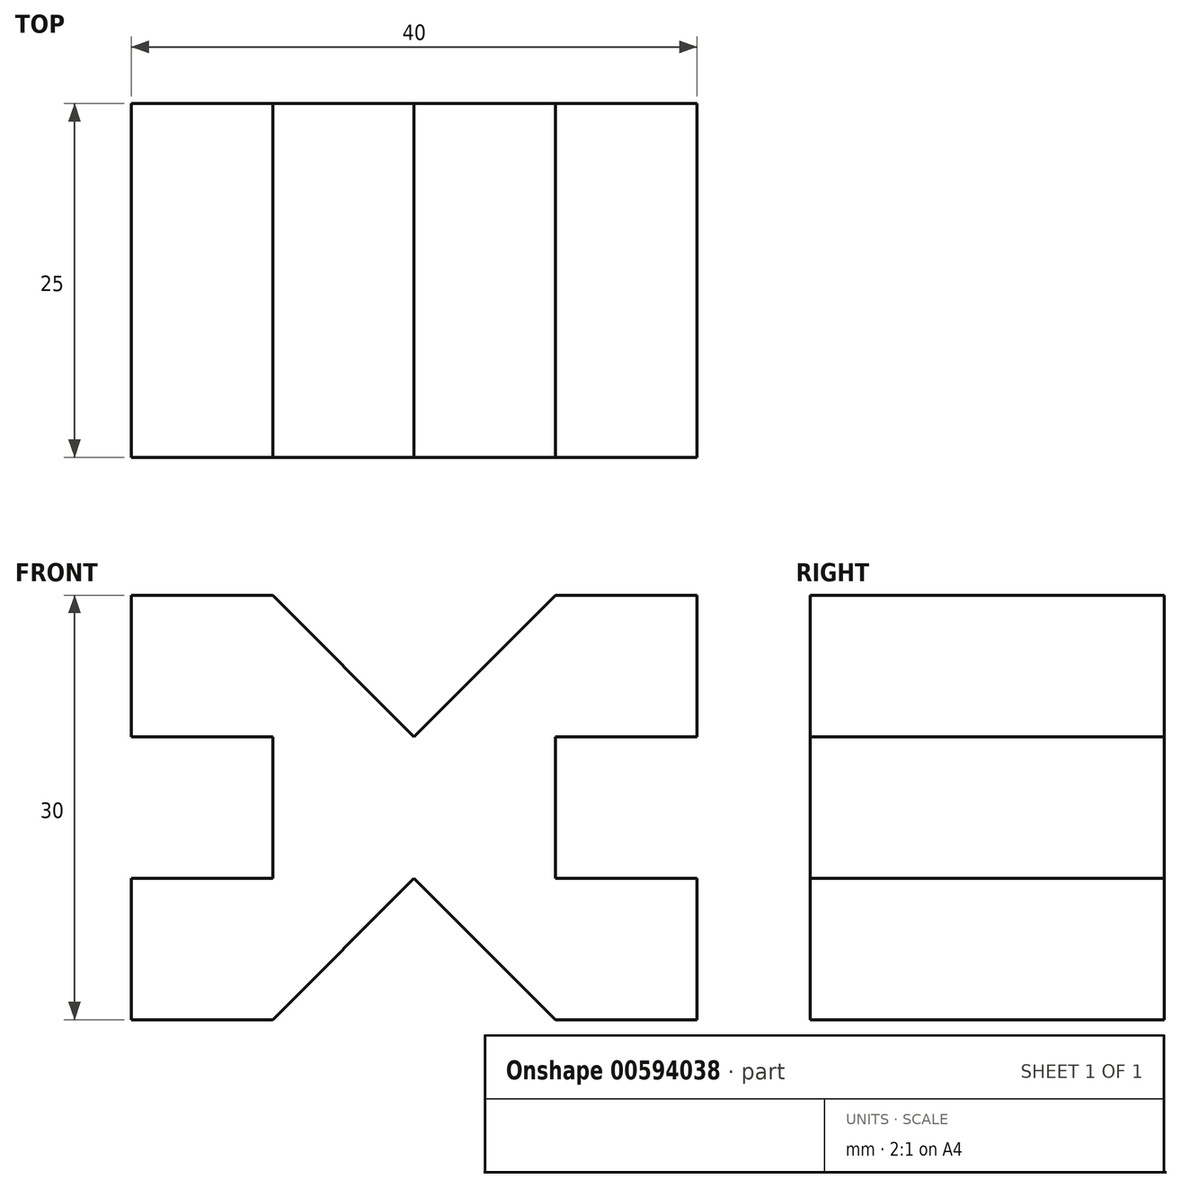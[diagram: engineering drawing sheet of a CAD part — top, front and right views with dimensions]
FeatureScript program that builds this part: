
annotation { "Feature Type Name" : "Feature", "Feature Type Description" : "" }
export const myFeature = defineFeature(function(context is Context, id is Id, definition is map)
    precondition{}
    {
        {
            var Q0;
            Q0=qCreatedBy(makeId("Front.planeOp"),FACE);
            var sketch = newSketch(context, id + "F0", { "sketchPlane" : qUnion([Q0])});
            skLineSegment(sketch, "E0", {"start": v(0, 5) * mm, "end": v(-10, 15) * mm});
            skLineSegment(sketch, "E1", {"start": v(-10, 15) * mm, "end": v(-20, 15) * mm});
            skLineSegment(sketch, "E2", {"start": v(-20, 15) * mm, "end": v(-20, 5) * mm});
            skLineSegment(sketch, "E3", {"start": v(-20, 5) * mm, "end": v(-10, 5) * mm});
            skLineSegment(sketch, "E4", {"start": v(-10, 5) * mm, "end": v(-10, 0) * mm});
            skLineSegment(sketch, "E5.MirrorCS", {"start": v(0, -5) * mm, "end": v(-10, -15) * mm});
            skLineSegment(sketch, "E6.MirrorCS", {"start": v(-20, -5) * mm, "end": v(-10, -5) * mm});
            skLineSegment(sketch, "E7.MirrorCS", {"start": v(-20, -15) * mm, "end": v(-20, -5) * mm});
            skLineSegment(sketch, "E8.MirrorCS", {"start": v(-10, -5) * mm, "end": v(-10, 0) * mm});
            skLineSegment(sketch, "E9.MirrorCS", {"start": v(-10, -15) * mm, "end": v(-20, -15) * mm});
            skLineSegment(sketch, "E10.MirrorCS", {"start": v(10, 5) * mm, "end": v(10, 0) * mm});
            skLineSegment(sketch, "E11.MirrorCS", {"start": v(10, -5) * mm, "end": v(10, 0) * mm});
            skLineSegment(sketch, "E12.MirrorCS", {"start": v(0, -5) * mm, "end": v(10, -15) * mm});
            skLineSegment(sketch, "E13.MirrorCS", {"start": v(20, -5) * mm, "end": v(10, -5) * mm});
            skLineSegment(sketch, "E14.MirrorCS", {"start": v(20, -15) * mm, "end": v(20, -5) * mm});
            skLineSegment(sketch, "E15.MirrorCS", {"start": v(0, 5) * mm, "end": v(10, 15) * mm});
            skLineSegment(sketch, "E16.MirrorCS", {"start": v(10, 15) * mm, "end": v(20, 15) * mm});
            skLineSegment(sketch, "E17.MirrorCS", {"start": v(10, -15) * mm, "end": v(20, -15) * mm});
            skLineSegment(sketch, "E18.MirrorCS", {"start": v(20, 5) * mm, "end": v(10, 5) * mm});
            skLineSegment(sketch, "E19.MirrorCS", {"start": v(20, 15) * mm, "end": v(20, 5) * mm});
            skSolve(sketch);
        }
        {
            var Q0;
            Q0=makeQuery(id+"F0.imprint","IMPRINT",FACE,{"disambiguationData":[TD([[makeQuery(id+"F0.imprint","IMPRINT",EDGE,{"derivedFrom":sQuery(id+"F0.wireOp",EDGE,"E0")}),1.0]])]});
            extrude(context, id + "F1", {"entities" : qUnion([Q0]), "depth" : 25 * mm, "offsetDistance" : 25 * mm});
        }
    });
